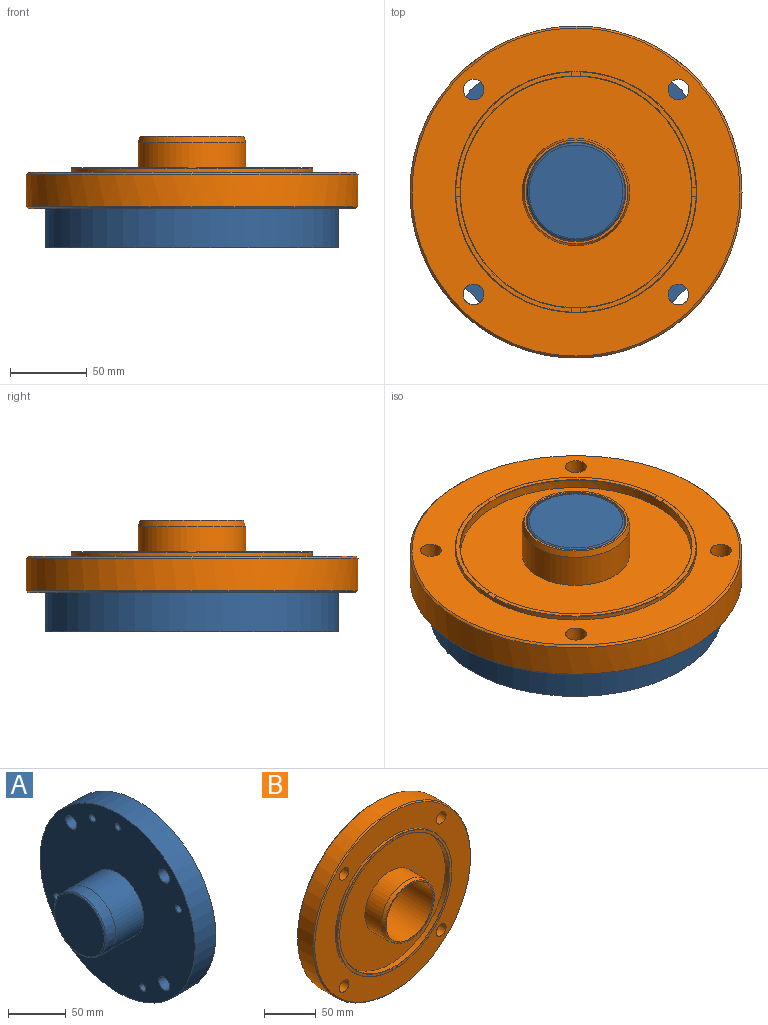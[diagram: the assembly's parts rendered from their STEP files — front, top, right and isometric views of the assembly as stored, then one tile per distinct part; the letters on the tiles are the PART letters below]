
ASSEMBLY  parts=2 mates=1
PART A: 44 faces, bbox 72.4x190.5x190.5 mm
  f0: plane 190.5x190.5mm, normal (1,0,0), area 26833.6mm2, adj f1,f7,f8,f9,f10,f11,f15,f18
  f1: cylinder r=95.25mm len=190.5mm, axis (1,0,0), area 15201.2mm2, adj f0,f2
  f2: plane 190.5x190.5mm, normal (-1,0,0), area 24495.7mm2, adj f1,f3,f7,f8,f9,f10,f16,f19
  f3: cylinder r=32.13mm len=64.26mm, axis (1,0,0), area 6922.6mm2, adj f2,f4
  f4: cone r=31.73mm half-angle=2deg, axis (1,0,0), area 2303.5mm2, adj f3,f5
  f5: torus R=30.46mm, axis (1,0,0), area 383.1mm2, adj f4,f6
  f6: plane 60.92x60.92mm, normal (-1,0,0), area 2915mm2, adj f5
  f7: cylinder r=6.74mm len=25.4mm, axis (-1,0,0), area 1076.2mm2, adj f0,f2
  f8: cylinder r=6.74mm len=25.4mm, axis (-1,0,0), area 1076.2mm2, adj f0,f2
  f9: cylinder r=6.74mm len=25.4mm, axis (-1,0,0), area 1076.2mm2, adj f0,f2
  f10: cylinder r=6.74mm len=25.4mm, axis (-1,0,0), area 1076.2mm2, adj f0,f2
  f11: cylinder r=12.7mm len=25.4mm, axis (1,0,0), area 202.7mm2, adj f0,f12
  f12: plane 25.4x25.4mm, normal (1,0,0), area 221.7mm2, adj f11,f13
  f13: cylinder r=9.53mm len=60.95mm, axis (1,0,0), area 3647.8mm2, adj f12,f14
  f14: cone r=0mm half-angle=59deg, axis (1,0,0), area 332.5mm2, adj f13
  f15: cylinder r=5.36mm len=10.72mm, axis (-1,0,0), area 333.6mm2, adj f0,f17
  f16: cylinder r=3.57mm len=15.49mm, axis (-1,0,0), area 347.4mm2, adj f2,f17
  f17: plane 10.72x10.72mm, normal (1,0,0), area 50.2mm2, adj f15,f16
  f18: cylinder r=5.36mm len=10.72mm, axis (-1,0,0), area 333.6mm2, adj f0,f20
  f19: cylinder r=3.57mm len=15.49mm, axis (-1,0,0), area 347.4mm2, adj f2,f20
  f20: plane 10.72x10.72mm, normal (1,0,0), area 50.2mm2, adj f18,f19
  f21: cylinder r=5.36mm len=10.72mm, axis (-1,0,0), area 333.6mm2, adj f0,f23
  f22: cylinder r=3.57mm len=15.49mm, axis (-1,0,0), area 347.4mm2, adj f2,f23
  f23: plane 10.72x10.72mm, normal (1,0,0), area 50.2mm2, adj f21,f22
  f24: cylinder r=5.36mm len=10.72mm, axis (-1,0,0), area 333.6mm2, adj f0,f26
  f25: cylinder r=3.57mm len=15.49mm, axis (-1,0,0), area 347.4mm2, adj f2,f26
  f26: plane 10.72x10.72mm, normal (1,0,0), area 50.2mm2, adj f24,f25
  f27: cone r=3.17mm half-angle=59deg, axis (1,0,0), area 36.9mm2, adj f28
  f28: cylinder r=3.17mm len=6.35mm, axis (-1,0,0), area 61.8mm2, adj f27,f29
  f29: plane 7.94x7.94mm, normal (1,0,0), area 17.8mm2, adj f28,f30
  f30: cylinder r=3.97mm len=17.48mm, axis (-1,0,0), area 435.8mm2, adj f0,f29
  f31: cone r=3.17mm half-angle=59deg, axis (1,0,0), area 36.9mm2, adj f32
  f32: cylinder r=3.17mm len=6.35mm, axis (-1,0,0), area 61.8mm2, adj f31,f33
  f33: plane 7.94x7.94mm, normal (1,0,0), area 17.8mm2, adj f32,f34
  f34: cylinder r=3.97mm len=17.48mm, axis (-1,0,0), area 435.8mm2, adj f0,f33
  f35: cone r=3.17mm half-angle=59deg, axis (1,0,0), area 36.9mm2, adj f36
  f36: cylinder r=3.17mm len=6.35mm, axis (-1,0,0), area 61.8mm2, adj f35,f37
  f37: plane 7.94x7.94mm, normal (1,0,0), area 17.8mm2, adj f36,f38
  f38: cylinder r=3.97mm len=17.48mm, axis (-1,0,0), area 435.8mm2, adj f0,f37
  f39: cone r=3.17mm half-angle=59deg, axis (1,0,0), area 36.9mm2, adj f40
  f40: cylinder r=3.17mm len=6.35mm, axis (-1,0,0), area 61.8mm2, adj f39,f41
  f41: plane 7.94x7.94mm, normal (1,0,0), area 17.8mm2, adj f40,f42
  f42: cylinder r=3.97mm len=17.48mm, axis (-1,0,0), area 435.8mm2, adj f0,f41
  f43: cylinder r=3.17mm len=25.4mm, axis (-1,0,0), area 506.7mm2, adj f0,f2
PART B: 42 faces, bbox 215.9x47x215.9 mm
  f0: plane 74.95x74.95mm, normal (0,-1,0), area 305.1mm2, adj f1,f2,f36,f38
  f1: cone r=78.45mm half-angle=45deg, axis (0,1,0), area 41.9mm2, adj f0,f13,f36,f38
  f2: cone r=75.53mm half-angle=45deg, axis (0,-1,0), area 40.3mm2, adj f0,f15,f36,f38
  f3: plane 74.95x74.95mm, normal (0,-1,0), area 305.1mm2, adj f4,f5,f33,f35
  f4: cone r=78.45mm half-angle=45deg, axis (0,1,0), area 41.9mm2, adj f3,f13,f33,f35
  f5: cone r=75.53mm half-angle=45deg, axis (0,-1,0), area 40.3mm2, adj f3,f15,f33,f35
  f6: plane 74.95x74.95mm, normal (0,-1,0), area 305.1mm2, adj f7,f8,f30,f32
  f7: cone r=78.45mm half-angle=45deg, axis (0,1,0), area 41.9mm2, adj f6,f13,f30,f32
  f8: cone r=75.53mm half-angle=45deg, axis (0,-1,0), area 40.3mm2, adj f6,f15,f30,f32
  f9: plane 213.36x213.36mm, normal (0,1,0), area 31808.9mm2, adj f20,f22,f23,f24,f25,f41
  f10: plane 213.36x213.36mm, normal (0,-1,0), area 15848.2mm2, adj f13,f21,f22,f23,f24,f25
  f11: cylinder r=32.13mm len=64.26mm, axis (0,1,0), area 9307.1mm2, adj f28,f41
  f12: cylinder r=107.95mm len=215.9mm, axis (0,1,0), area 14299.3mm2, adj f20,f21
  f13: cylinder r=78.45mm len=156.9mm, axis (0,1,0), area 1314.6mm2, adj f1,f4,f7,f10,f26,f31,f34,f37
  f14: plane 74.95x74.95mm, normal (0,-1,0), area 305.1mm2, adj f26,f27,f29,f39
  f15: cylinder r=75.27mm len=150.55mm, axis (0,1,0), area 2763mm2, adj f2,f5,f8,f16,f27,f31,f34,f37
  f16: plane 150.55x150.55mm, normal (0,-1,0), area 13968.3mm2, adj f15,f17
  f17: cylinder r=34.92mm len=69.85mm, axis (0,1,0), area 4888.5mm2, adj f16,f18
  f18: cone r=34.92mm half-angle=15deg, axis (0,1,0), area 953.2mm2, adj f17,f19
  f19: plane 67.56x67.56mm, normal (0,-1,0), area 290.4mm2, adj f18,f28
  f20: cone r=106.68mm half-angle=45deg, axis (0,-1,0), area 1211mm2, adj f9,f12
  f21: cone r=107.95mm half-angle=45deg, axis (0,1,0), area 1211mm2, adj f10,f12
  f22: cylinder r=6.74mm len=23.62mm, axis (0,1,0), area 1000.9mm2, adj f9,f10
  f23: cylinder r=6.74mm len=23.62mm, axis (0,1,0), area 1000.9mm2, adj f9,f10
  f24: cylinder r=6.74mm len=23.62mm, axis (0,1,0), area 1000.9mm2, adj f9,f10
  f25: cylinder r=6.74mm len=23.62mm, axis (0,1,0), area 1000.9mm2, adj f9,f10
  f26: cone r=78.45mm half-angle=45deg, axis (0,1,0), area 41.9mm2, adj f13,f14,f29,f39
  f27: cone r=75.53mm half-angle=45deg, axis (0,-1,0), area 40.3mm2, adj f14,f15,f29,f39
  f28: cone r=32.38mm half-angle=45deg, axis (0,-1,0), area 72.8mm2, adj f11,f19
  f29: plane 3.18x0.25mm, normal (0,0,-1), area 0.7mm2, adj f14,f26,f27,f31
  f30: plane 3.18x0.25mm, normal (0,0,1), area 0.7mm2, adj f6,f7,f8,f31
  f31: plane 6.35x3.24mm, normal (0,-1,0), area 20.2mm2, adj f13,f15,f29,f30
  f32: plane 3.18x0.25mm, normal (-1,0,0), area 0.7mm2, adj f6,f7,f8,f34
  f33: plane 3.18x0.25mm, normal (1,0,0), area 0.7mm2, adj f3,f4,f5,f34
  f34: plane 6.35x3.24mm, normal (0,-1,0), area 20.2mm2, adj f13,f15,f32,f33
  f35: plane 3.18x0.25mm, normal (0,0,1), area 0.7mm2, adj f3,f4,f5,f37
  f36: plane 3.18x0.25mm, normal (0,0,-1), area 0.7mm2, adj f0,f1,f2,f37
  f37: plane 6.35x3.24mm, normal (0,-1,0), area 20.2mm2, adj f13,f15,f35,f36
  f38: plane 3.18x0.25mm, normal (1,0,0), area 0.7mm2, adj f0,f1,f2,f40
  f39: plane 3.18x0.25mm, normal (-1,0,0), area 0.7mm2, adj f14,f26,f27,f40
  f40: plane 6.35x3.24mm, normal (0,-1,0), area 20.2mm2, adj f13,f15,f38,f39
  f41: cone r=32.13mm half-angle=45deg, axis (0,1,0), area 183.1mm2, adj f9,f11
PLACE A rot(axis=(-0.58,0.58,0.58),120deg) t=(0,-80.82,0)mm
PLACE B rot(axis=(-0.58,0.58,-0.58),120deg) t=(0,-80.93,0)mm
MATE slider A.f2 <-> B.f1  axis (0,0,1) through (0,-80.93,0)mm
